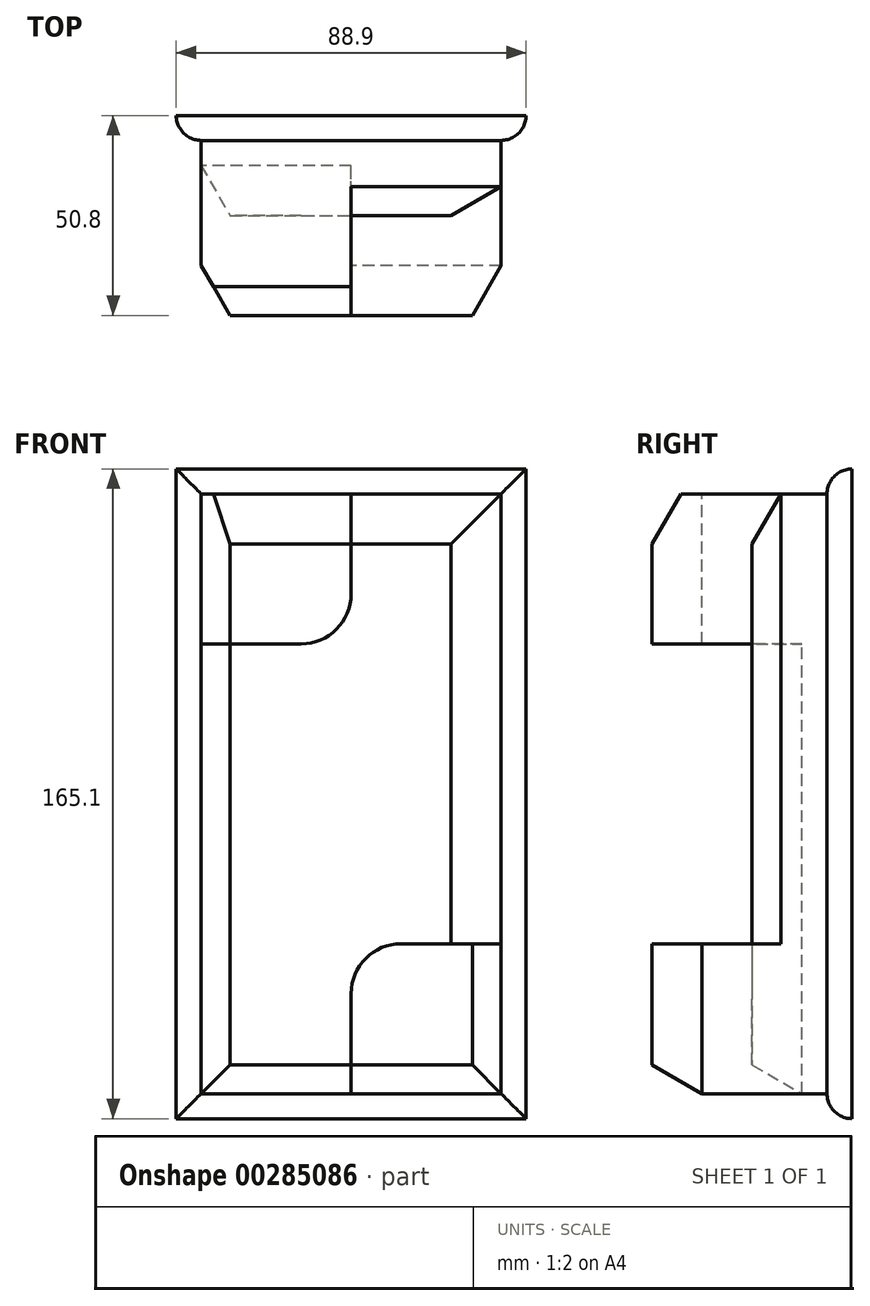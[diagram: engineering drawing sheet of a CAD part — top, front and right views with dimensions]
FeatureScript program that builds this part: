
annotation { "Feature Type Name" : "Feature", "Feature Type Description" : "" }
export const myFeature = defineFeature(function(context is Context, id is Id, definition is map)
    precondition{}
    {
        {
            var Q0;
            Q0=qCreatedBy(makeId("Front.planeOp"),FACE);
            var sketch = newSketch(context, id + "F0", { "sketchPlane" : qUnion([Q0])});
            skLineSegment(sketch, "E0.bottom", {"start": v(-29.9, 76.95) * mm, "end": v(46.3, 76.95) * mm});
            skLineSegment(sketch, "E0.top", {"start": v(-29.9, -75.45) * mm, "end": v(46.3, -75.45) * mm});
            skLineSegment(sketch, "E0.left", {"start": v(-29.9, 76.95) * mm, "end": v(-29.9, -75.45) * mm});
            skLineSegment(sketch, "E0.right", {"start": v(46.3, 76.95) * mm, "end": v(46.3, -75.45) * mm});
            skLineSegment(sketch, "E1.0", {"start": v(-36.25, 83.3) * mm, "end": v(52.65, 83.3) * mm});
            skLineSegment(sketch, "E1.1", {"start": v(-36.25, 83.3) * mm, "end": v(-36.25, -81.8) * mm});
            skLineSegment(sketch, "E1.2", {"start": v(-36.25, -81.8) * mm, "end": v(52.65, -81.8) * mm});
            skLineSegment(sketch, "E1.3", {"start": v(52.65, 83.3) * mm, "end": v(52.65, -81.8) * mm});
            skLineSegment(sketch, "E2", {"start": v(8.2, 76.95) * mm, "end": v(8.2, 51.55) * mm});
            skLineSegment(sketch, "E3", {"start": v(-4.5, 38.85) * mm, "end": v(-29.9, 38.85) * mm});
            skLineSegment(sketch, "E4", {"start": v(8.2, -75.45) * mm, "end": v(8.2, -50.05) * mm});
            skLineSegment(sketch, "E5", {"start": v(20.9, -37.35) * mm, "end": v(46.3, -37.35) * mm});
            skPoint(sketch, "E6.visualSharp", {"position": v(8.2, 38.85) * mm});
            skArc(sketch, "E6.filletArc", {"start": v(-4.5, 38.85) * mm, "mid": v(4.48, 42.57) * mm, "end": v(8.2, 51.55) * mm});
            skPoint(sketch, "E7.visualSharp", {"position": v(8.2, -37.35) * mm});
            skArc(sketch, "E7.filletArc", {"start": v(20.9, -37.35) * mm, "mid": v(11.92, -41.07) * mm, "end": v(8.2, -50.05) * mm});
            skSolve(sketch);
        }
        {
            var Q0;
            Q0 = qSketchRegion(id + "F0", true);
            extrude(context, id + "F1", {"entities" : qUnion([Q0]), "depth" : 6.35 * mm});
        }
        {
            var Q0;
            {var subQ9=sQuery(id+"F0.wireOp",EDGE,"E2");Q0=makeQuery(id+"F0.imprint","IMPRINT",FACE,{"disambiguationData":[TD([[makeQuery(id+"F0.imprint","IMPRINT",EDGE,{"derivedFrom":subQ9}),1.0]])]});}
            extrude(context, id + "F2", {"entities" : qUnion([Q0]), "operationType" : NewBodyOperationType.ADD, "depth" : 25.4 * mm});
        }
        {
            var Q0;
            {var subQ1=sQuery(id+"F0.wireOp",EDGE,"E2");Q0=makeQuery(id+"F0.imprint","IMPRINT",FACE,{"disambiguationData":[TD([[makeQuery(id+"F0.imprint","IMPRINT",EDGE,{"derivedFrom":subQ1}),-1.0]])]});}
            var Q1;
            {var subQ1=sQuery(id+"F0.wireOp",EDGE,"E4");Q1=makeQuery(id+"F0.imprint","IMPRINT",FACE,{"disambiguationData":[TD([[makeQuery(id+"F0.imprint","IMPRINT",EDGE,{"derivedFrom":subQ1}),-1.0]])]});}
            extrude(context, id + "F3", {"entities" : qUnion([Q0, Q1]), "operationType" : NewBodyOperationType.ADD, "depth" : 50.8 * mm});
        }
        {
            var Q0;
            Q0=makeQuery(id+"F1.opExtrude","CAP_EDGE",EDGE,{"disambiguationData":[OSD([sQuery(id+"F0.wireOp",EDGE,"E1.0")])],"isStart":false});
            var Q1;
            Q1=makeQuery(id+"F1.opExtrude","CAP_EDGE",EDGE,{"disambiguationData":[OSD([sQuery(id+"F0.wireOp",EDGE,"E1.1")])],"isStart":false});
            var Q2;
            Q2=makeQuery(id+"F1.opExtrude","CAP_EDGE",EDGE,{"disambiguationData":[OSD([sQuery(id+"F0.wireOp",EDGE,"E1.2")])],"isStart":false});
            var Q3;
            Q3=makeQuery(id+"F1.opExtrude","CAP_EDGE",EDGE,{"disambiguationData":[OSD([sQuery(id+"F0.wireOp",EDGE,"E1.3")])],"isStart":false});
            fillet(context, id + "F4", {"entities" : qUnion([Q0, Q1, Q2, Q3]), "radius" : 6.35 * mm, "tangentPropagation" : true, "allowEdgeOverflow" : false});
        }
        {
            var Q0;
            Q0=makeQuery(id+"F3.opExtrude","CAP_EDGE",EDGE,{"disambiguationData":[OSD([sQuery(id+"F0.wireOp",EDGE,"E0.top")])],"isStart":false});
            var Q1;
            Q1=makeQuery(id+"F2.opExtrude","CAP_EDGE",EDGE,{"disambiguationData":[OSD([sQuery(id+"F0.wireOp",EDGE,"E0.top")])],"isStart":false});
            var Q2;
            Q2=makeQuery(id+"F2.opExtrude","CAP_EDGE",EDGE,{"disambiguationData":[OSD([sQuery(id+"F0.wireOp",EDGE,"E0.left")])],"isStart":false});
            var Q3;
            Q3=makeQuery(id+"F3.opExtrude","CAP_EDGE",EDGE,{"disambiguationData":[OSD([sQuery(id+"F0.wireOp",EDGE,"E0.left")])],"isStart":false});
            var Q4;
            Q4=makeQuery(id+"F3.opExtrude","CAP_EDGE",EDGE,{"disambiguationData":[OSD([sQuery(id+"F0.wireOp",EDGE,"E0.right")])],"isStart":false});
            var Q5;
            Q5=makeQuery(id+"F3.opExtrude","CAP_EDGE",EDGE,{"disambiguationData":[OSD([sQuery(id+"F0.wireOp",EDGE,"E0.bottom")])],"isStart":false});
            var Q6;
            Q6=makeQuery(id+"F2.opExtrude","CAP_EDGE",EDGE,{"disambiguationData":[OSD([sQuery(id+"F0.wireOp",EDGE,"E0.right")])],"isStart":false});
            var Q7;
            Q7=makeQuery(id+"F2.opExtrude","CAP_EDGE",EDGE,{"disambiguationData":[OSD([sQuery(id+"F0.wireOp",EDGE,"E0.bottom")])],"isStart":false});
            chamfer(context, id + "F5", {"entities" : qUnion([Q0, Q1, Q2, Q3, Q4, Q5, Q6, Q7]), "chamferType" : ChamferType.OFFSET_ANGLE, "width" : 12.7 * mm, "oppositeDirection" : true, "angle" : 30 * degree, "tangentPropagation" : true});
        }
    });
